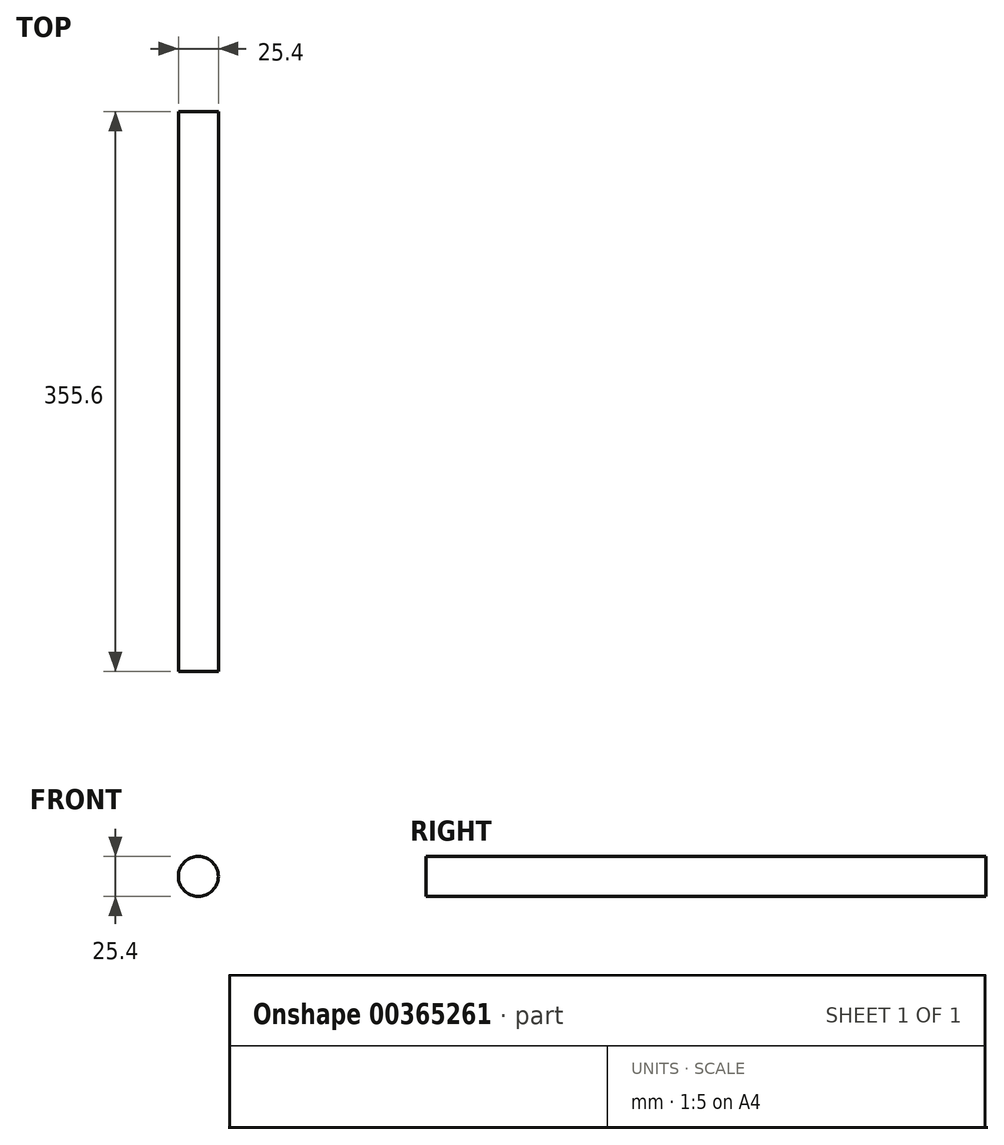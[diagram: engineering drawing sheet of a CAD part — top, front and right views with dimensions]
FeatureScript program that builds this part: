
annotation { "Feature Type Name" : "Feature", "Feature Type Description" : "" }
export const myFeature = defineFeature(function(context is Context, id is Id, definition is map)
    precondition{}
    {
        {
            var Q0;
            Q0=qCreatedBy(makeId("Front.planeOp"),FACE);
            var sketch = newSketch(context, id + "F0", { "sketchPlane" : qUnion([Q0])});
            skCircle(sketch, "E0", {"center": v(-7.68, 6.51) * mm, "radius": 12.7 * mm});
            skSolve(sketch);
        }
        {
            var Q0;
            Q0=qSketchRegion(id+"F0",true);
            extrude(context, id + "F1", {"entities" : qUnion([Q0]), "depth" : 355.6 * mm});
        }
    });
